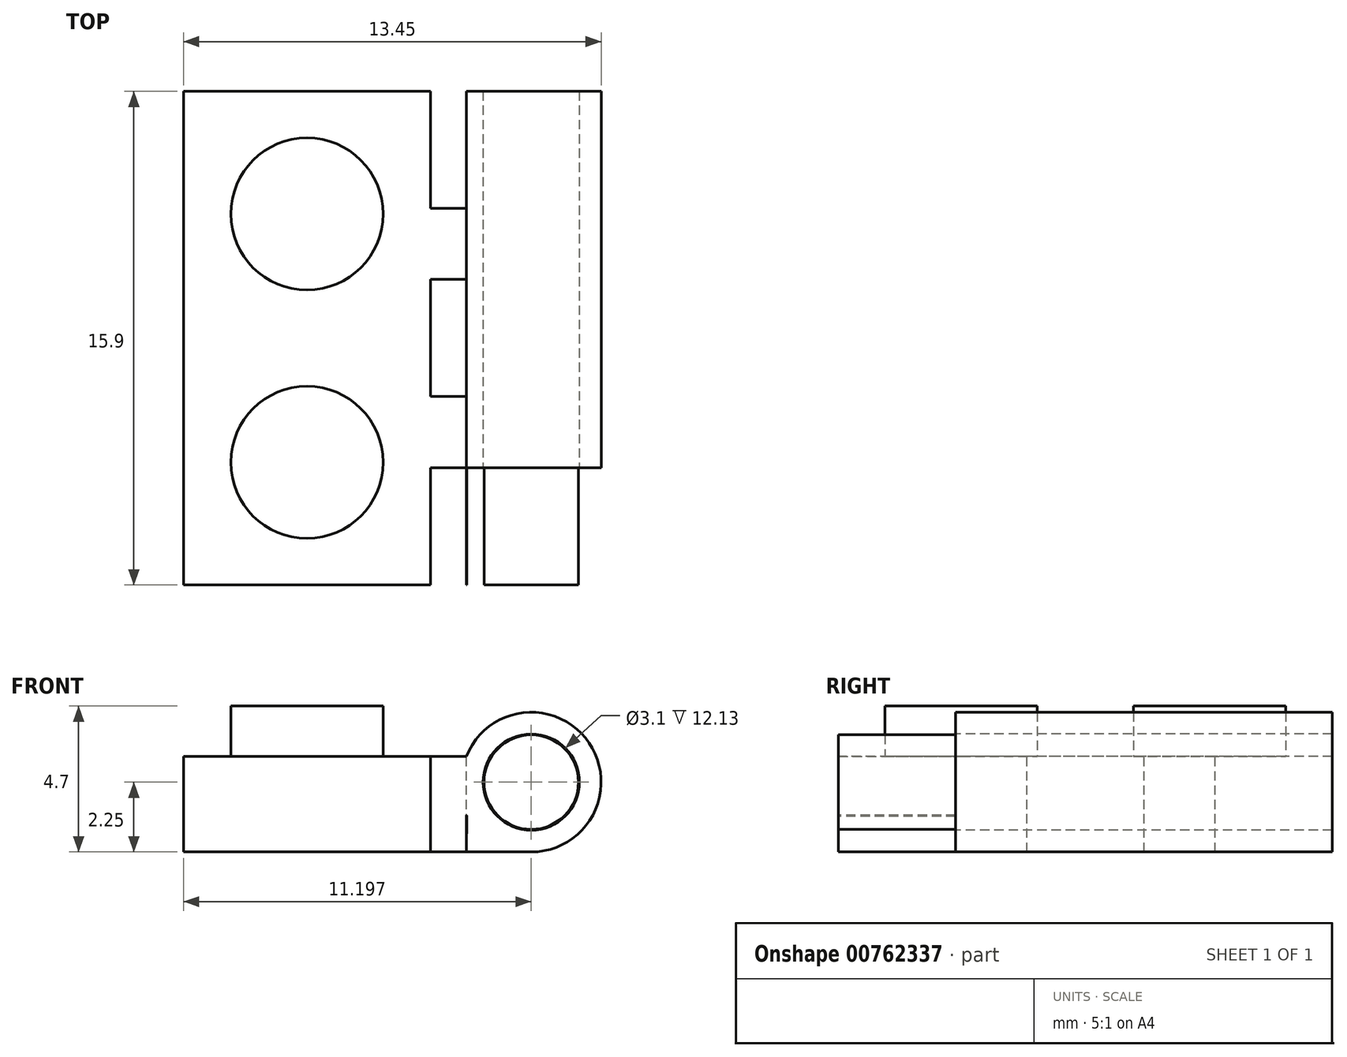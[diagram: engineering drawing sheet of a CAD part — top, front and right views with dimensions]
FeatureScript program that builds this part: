
annotation { "Feature Type Name" : "Feature", "Feature Type Description" : "" }
export const myFeature = defineFeature(function(context is Context, id is Id, definition is map)
    precondition{}
    {
        {
            var Q0;
            Q0=qCreatedBy(makeId("Top.planeOp"),FACE);
            var sketch = newSketch(context, id + "F0", { "sketchPlane" : qUnion([Q0])});
            skLineSegment(sketch, "E0.bottom", {"start": v(0, 0) * mm, "end": v(7.95, 0) * mm});
            skLineSegment(sketch, "E0.top", {"start": v(0, -15.9) * mm, "end": v(7.95, -15.9) * mm});
            skLineSegment(sketch, "E0.left", {"start": v(0, 0) * mm, "end": v(0, -15.9) * mm});
            skLineSegment(sketch, "E0.right", {"start": v(7.95, 0) * mm, "end": v(7.95, -15.9) * mm});
            skCircle(sketch, "E1", {"center": v(3.98, -3.95) * mm, "radius": 2.45 * mm});
            skPoint(sketch, "E1.centerSnap0", {"position": v(3.98, 0) * mm});
            skCircle(sketch, "E2", {"center": v(3.98, -11.95) * mm, "radius": 2.45 * mm});
            skSolve(sketch);
        }
        {
            var Q0;
            Q0=qSketchRegion(id+"F0",true);
            extrude(context, id + "F1", {"entities" : qUnion([Q0]), "depth" : 3.08 * mm, "offsetDistance" : 25 * mm});
        }
        {
            var Q0;
            Q0=makeQuery(id+"F0.imprint","IMPRINT",FACE,{"disambiguationData":[TD([[makeQuery(id+"F0.imprint","IMPRINT",EDGE,{"derivedFrom":sQuery(id+"F0.wireOp",EDGE,"E2")}),1.0]])]});
            var Q1;
            Q1=makeQuery(id+"F0.imprint","IMPRINT",FACE,{"disambiguationData":[TD([[makeQuery(id+"F0.imprint","IMPRINT",EDGE,{"derivedFrom":sQuery(id+"F0.wireOp",EDGE,"E1")}),1.0]])]});
            extrude(context, id + "F2", {"entities" : qUnion([Q0, Q1]), "operationType" : NewBodyOperationType.ADD, "depth" : 4.7 * mm, "offsetDistance" : 25 * mm});
        }
        {
            var Q0;
            Q0=makeQuery(id+"F1.opExtrude","SWEPT_FACE",FACE,{"disambiguationData":[OSD([sQuery(id+"F0.wireOp",EDGE,"E0.top")])]});
            var sketch = newSketch(context, id + "F3", { "sketchPlane" : qUnion([Q0])});
            skArc(sketch, "E3", {"start": v(11.2, 0) * mm, "mid": v(13.06, 3.51) * mm, "end": v(9.1, 3.08) * mm});
            skLineSegment(sketch, "E4", {"start": v(7.95, 0) * mm, "end": v(11.2, 0) * mm});
            skLineSegment(sketch, "E5", {"start": v(7.95, 3.08) * mm, "end": v(9.1, 3.08) * mm});
            skCircle(sketch, "E6", {"center": v(11.2, 2.25) * mm, "radius": 1.55 * mm});
            skSolve(sketch);
        }
        {
            var Q0;
            Q0=makeQuery(id+"F3.imprint","IMPRINT",FACE,{"disambiguationData":[TD([[makeQuery(id+"F3.imprint","IMPRINT",EDGE,{"derivedFrom":sQuery(id+"F3.wireOp",EDGE,"E3")}),1.0]])]});
            extrude(context, id + "F4", {"entities" : qUnion([Q0]), "operationType" : NewBodyOperationType.ADD, "oppositeDirection" : true, "depth" : 15.9 * mm, "offsetDistance" : 25 * mm});
        }
        {
            var Q0;
            Q0=makeQuery(id+"F4.boolean.opBoolean","MERGE",FACE,{"derivedFrom":[makeQuery(id+"F1.opExtrude","CAP_FACE",FACE,{"disambiguationData":[OSD([sQuery(id+"F0.wireOp",EDGE,"E0.bottom"),sQuery(id+"F0.wireOp",EDGE,"E0.top"),sQuery(id+"F0.wireOp",EDGE,"E0.left"),sQuery(id+"F0.wireOp",EDGE,"E0.right"),sQuery(id+"F0.wireOp",EDGE,"E1"),sQuery(id+"F0.wireOp",EDGE,"E2")])],"isStart":false}),makeQuery(id+"F4.opExtrude","SWEPT_FACE",FACE,{"disambiguationData":[OSD([sQuery(id+"F3.wireOp",EDGE,"E5")])]})]});
            var sketch = newSketch(context, id + "F5", { "sketchPlane" : qUnion([Q0])});
            skPoint(sketch, "E7", {"position": v(7.95, 0) * mm});
            skLineSegment(sketch, "E8", {"start": v(7.95, 0) * mm, "end": v(7.95, -3.77) * mm});
            skLineSegment(sketch, "E9", {"start": v(7.95, -3.77) * mm, "end": v(9.1, -3.77) * mm});
            skLineSegment(sketch, "E10", {"start": v(9.1, -3.77) * mm, "end": v(9.1, 0) * mm});
            skLineSegment(sketch, "E11", {"start": v(9.1, 0) * mm, "end": v(7.95, 0) * mm});
            skLineSegment(sketch, "E12", {"start": v(7.95, -6.06) * mm, "end": v(9.1, -6.06) * mm});
            skLineSegment(sketch, "E13", {"start": v(9.1, -6.06) * mm, "end": v(9.1, -9.83) * mm});
            skLineSegment(sketch, "E14", {"start": v(9.1, -9.83) * mm, "end": v(7.95, -9.83) * mm});
            skLineSegment(sketch, "E15", {"start": v(7.95, -9.83) * mm, "end": v(7.95, -6.06) * mm});
            skLineSegment(sketch, "E16", {"start": v(7.95, -15.9) * mm, "end": v(7.95, -12.13) * mm});
            skLineSegment(sketch, "E17", {"start": v(7.95, -12.13) * mm, "end": v(9.1, -12.13) * mm});
            skLineSegment(sketch, "E18", {"start": v(9.1, -12.13) * mm, "end": v(9.1, -15.9) * mm});
            skLineSegment(sketch, "E19", {"start": v(9.1, -15.9) * mm, "end": v(7.95, -15.9) * mm});
            skLineSegment(sketch, "E20", {"start": v(7.95, -3.77) * mm, "end": v(7.95, -6.06) * mm});
            skLineSegment(sketch, "E21", {"start": v(7.95, -12.13) * mm, "end": v(7.95, -9.83) * mm});
            skSolve(sketch);
        }
        {
            var Q0;
            Q0=qSketchRegion(id+"F5",true);
            extrude(context, id + "F6", {"entities" : qUnion([Q0]), "operationType" : NewBodyOperationType.REMOVE, "oppositeDirection" : true, "depth" : 25 * mm, "offsetDistance" : 25 * mm});
        }
        {
            var Q0;
            Q0=qSketchRegion(id+"F3",true);
            extrude(context, id + "F7", {"entities" : qUnion([Q0]), "oppositeDirection" : true, "depth" : 15.9 * mm, "offsetDistance" : 25 * mm});
        }
        {
            var Q0;
            {var subQ0=sQuery(id+"F3.wireOp",EDGE,"E3");var subQ3=sQuery(id+"F0.wireOp",EDGE,"E0.right");var subQ4=sQuery(id+"F0.wireOp",EDGE,"E0.top");var subQ5=sQuery(id+"F3.wireOp",EDGE,"E4");var subQ6=sQuery(id+"F3.wireOp",EDGE,"E6");Q0=makeQuery(id+"F6.boolean.opBoolean","SPLIT",FACE,{"disambiguationData":[TD([makeQuery(id+"F4.opExtrude","SWEPT_FACE",FACE,{"disambiguationData":[OSD([subQ0])]})])],"derivedFrom":makeQuery(id+"F4.boolean.opBoolean","MERGE",FACE,{"derivedFrom":[makeQuery(id+"F1.opExtrude","SWEPT_FACE",FACE,{"disambiguationData":[OSD([subQ4])]}),makeQuery(id+"F4.opExtrude","CAP_FACE",FACE,{"disambiguationData":[OSD([subQ4,subQ3,subQ0,subQ5,sQuery(id+"F3.wireOp",EDGE,"E5"),subQ6])],"isStart":true})]})});}
            var sketch = newSketch(context, id + "F8", { "sketchPlane" : qUnion([Q0])});
            skCircle(sketch, "E22", {"center": v(11.2, 2.25) * mm, "radius": 1.52 * mm});
            skArc(sketch, "E23", {"start": v(10.54, 0) * mm, "mid": v(12.68, 4.07) * mm, "end": v(9.12, 1.15) * mm});
            skLineSegment(sketch, "E24", {"start": v(9.12, 1.15) * mm, "end": v(9.1, 0) * mm});
            skLineSegment(sketch, "E25", {"start": v(9.1, 0) * mm, "end": v(10.54, 0) * mm});
            skSolve(sketch);
        }
        {
            var Q0;
            Q0 = qSketchRegion(id + "F8", true);
            extrude(context, id + "F9", {"entities" : qUnion([Q0]), "operationType" : NewBodyOperationType.REMOVE, "oppositeDirection" : true, "depth" : 3.77 * mm, "offsetDistance" : 25 * mm});
        }
    });
